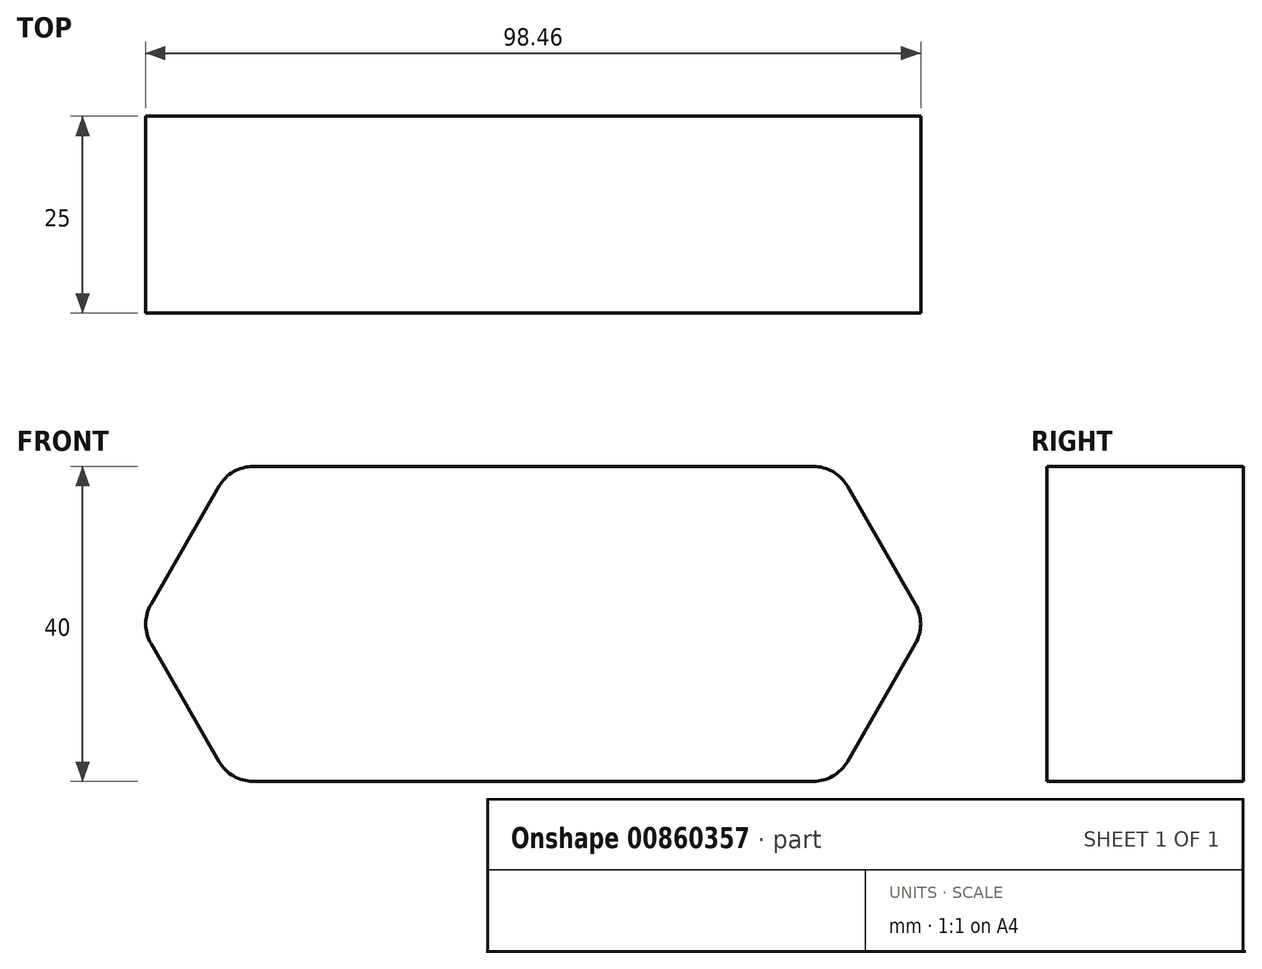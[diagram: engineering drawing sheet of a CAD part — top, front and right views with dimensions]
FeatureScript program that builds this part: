
annotation { "Feature Type Name" : "Feature", "Feature Type Description" : "" }
export const myFeature = defineFeature(function(context is Context, id is Id, definition is map)
    precondition{}
    {
        {
            var Q0;
            Q0=qCreatedBy(makeId("Front.planeOp"),FACE);
            var sketch = newSketch(context, id + "F0", { "sketchPlane" : qUnion([Q0])});
            skLineSegment(sketch, "E0", {"start": v(-50, 0) * mm, "end": v(-38.45, 20) * mm});
            skLineSegment(sketch, "E1", {"start": v(-38.45, 20) * mm, "end": v(0, 20) * mm});
            skLineSegment(sketch, "E2", {"start": v(-50, 0) * mm, "end": v(0, 0) * mm, "construction": true});
            skLineSegment(sketch, "E3", {"start": v(0, 0) * mm, "end": v(0, 20) * mm, "construction": true});
            skLineSegment(sketch, "E4.MirrorCS", {"start": v(38.45, 20) * mm, "end": v(0, 20) * mm});
            skLineSegment(sketch, "E5.MirrorCS", {"start": v(50, 0) * mm, "end": v(38.45, 20) * mm});
            skLineSegment(sketch, "E6.MirrorCS", {"start": v(-50, 0) * mm, "end": v(-38.45, -20) * mm});
            skLineSegment(sketch, "E7.MirrorCS", {"start": v(-38.45, -20) * mm, "end": v(0, -20) * mm});
            skLineSegment(sketch, "E8.MirrorCS", {"start": v(38.45, -20) * mm, "end": v(0, -20) * mm});
            skLineSegment(sketch, "E9.MirrorCS", {"start": v(50, 0) * mm, "end": v(38.45, -20) * mm});
            skSolve(sketch);
        }
        {
            var Q0;
            Q0 = qSketchRegion(id + "F0", true);
            extrude(context, id + "F1", {"entities" : qUnion([Q0]), "depth" : 25 * mm, "offsetDistance" : 25 * mm});
        }
        {
            var Q0;
            Q0=makeQuery(id+"F1.opExtrude","SWEPT_EDGE",EDGE,{"disambiguationData":[OSD([sQuery(id+"F0.wireOp",EDGE,"E0"),sQuery(id+"F0.wireOp",EDGE,"E1")])]});
            var Q1;
            Q1=makeQuery(id+"F1.opExtrude","SWEPT_EDGE",EDGE,{"disambiguationData":[OSD([sQuery(id+"F0.wireOp",EDGE,"E0"),sQuery(id+"F0.wireOp",EDGE,"E6.MirrorCS")])]});
            var Q2;
            Q2=makeQuery(id+"F1.opExtrude","SWEPT_EDGE",EDGE,{"disambiguationData":[OSD([sQuery(id+"F0.wireOp",EDGE,"E6.MirrorCS"),sQuery(id+"F0.wireOp",EDGE,"E7.MirrorCS")])]});
            var Q3;
            Q3=makeQuery(id+"F1.opExtrude","SWEPT_EDGE",EDGE,{"disambiguationData":[OSD([sQuery(id+"F0.wireOp",EDGE,"E4.MirrorCS"),sQuery(id+"F0.wireOp",EDGE,"E5.MirrorCS")])]});
            var Q4;
            Q4=makeQuery(id+"F1.opExtrude","SWEPT_EDGE",EDGE,{"disambiguationData":[OSD([sQuery(id+"F0.wireOp",EDGE,"E5.MirrorCS"),sQuery(id+"F0.wireOp",EDGE,"E9.MirrorCS")])]});
            var Q5;
            Q5=makeQuery(id+"F1.opExtrude","SWEPT_EDGE",EDGE,{"disambiguationData":[OSD([sQuery(id+"F0.wireOp",EDGE,"E8.MirrorCS"),sQuery(id+"F0.wireOp",EDGE,"E9.MirrorCS")])]});
            fillet(context, id + "F2", {"entities" : qUnion([Q0, Q1, Q2, Q3, Q4, Q5]), "radius" : 5 * mm, "tangentPropagation" : true, "allowEdgeOverflow" : false});
        }
    });
